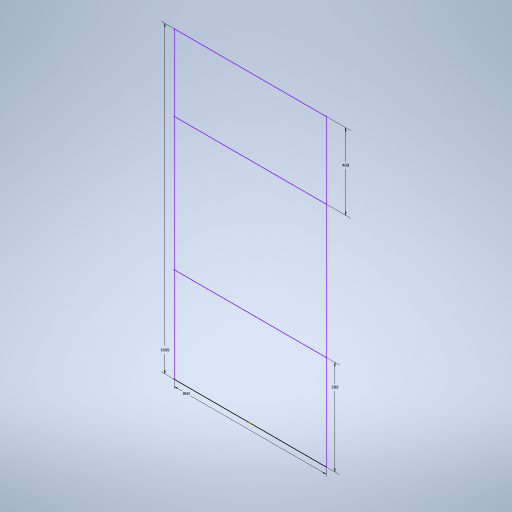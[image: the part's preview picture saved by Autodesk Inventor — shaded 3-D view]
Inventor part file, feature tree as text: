
AUTODESK INVENTOR PART (.ipt)
format: ipt  version: 2024.2 (Build 282272000, 272)  size: 238,592 bytes
history: native  units: in
note: dims shown in document units (in); Inventor stores cm internally (conversion verified against a paired STEP export)
features: sketch x2
ambient origin geometry x8: Origin, YZ Plane, XZ Plane, XY Plane, X Axis, Y Axis, Z Axis, Center Point
feature tree (2):
  sketch  "Sketch3"  dims[d5=31.4961in d6=62.9921in d7=15.748in d10=19.685in]
  sketch  "3D Sketch3"
